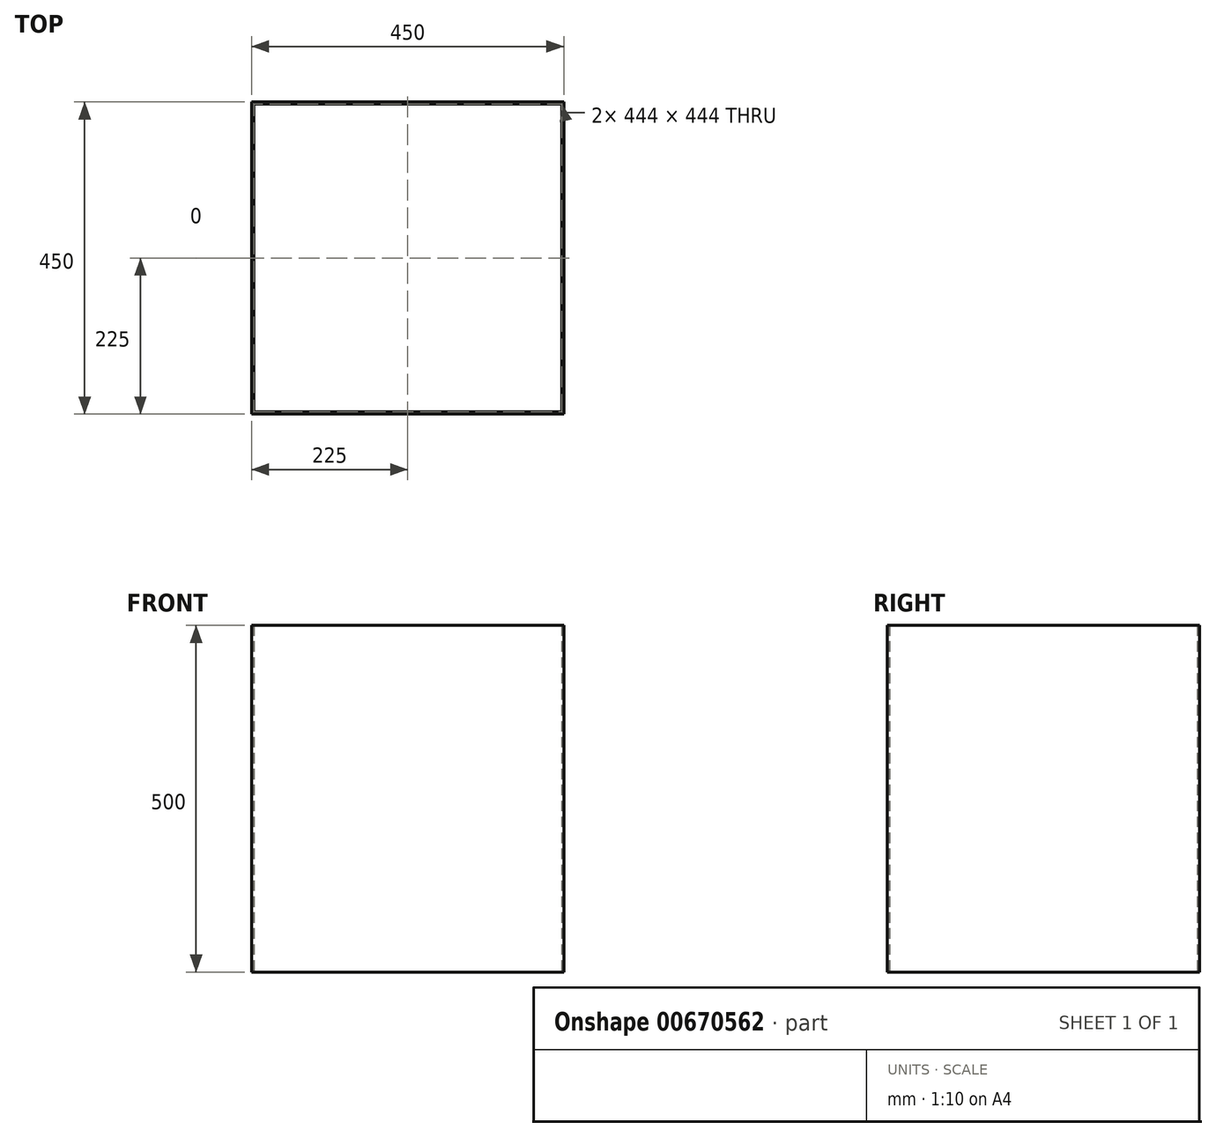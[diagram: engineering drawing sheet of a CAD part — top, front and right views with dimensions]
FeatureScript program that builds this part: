
annotation { "Feature Type Name" : "Feature", "Feature Type Description" : "" }
export const myFeature = defineFeature(function(context is Context, id is Id, definition is map)
    precondition{}
    {
        {
            var Q0;
            Q0=qCreatedBy(makeId("Top.planeOp"),FACE);
            var sketch = newSketch(context, id + "F0", { "sketchPlane" : qUnion([Q0])});
            skLineSegment(sketch, "E0.bottom", {"start": v(225, -225) * mm, "end": v(-225, -225) * mm});
            skLineSegment(sketch, "E0.top", {"start": v(225, 225) * mm, "end": v(-225, 225) * mm});
            skLineSegment(sketch, "E0.left", {"start": v(225, -225) * mm, "end": v(225, 225) * mm});
            skLineSegment(sketch, "E0.right", {"start": v(-225, -225) * mm, "end": v(-225, 225) * mm});
            skPoint(sketch, "E0.middle", {"position": v(0, 0) * mm});
            skLineSegment(sketch, "E1.0", {"start": v(222, 222) * mm, "end": v(-222, 222) * mm});
            skLineSegment(sketch, "E1.1", {"start": v(222, -222) * mm, "end": v(222, 222) * mm});
            skLineSegment(sketch, "E1.2", {"start": v(222, -222) * mm, "end": v(-222, -222) * mm});
            skLineSegment(sketch, "E1.3", {"start": v(-222, -222) * mm, "end": v(-222, 222) * mm});
            skLineSegment(sketch, "E2.0", {"start": v(-230, -230) * mm, "end": v(-230, 225) * mm});
            skLineSegment(sketch, "E2.1", {"start": v(230, -230) * mm, "end": v(-230, -230) * mm});
            skLineSegment(sketch, "E2.2", {"start": v(230, -230) * mm, "end": v(230, 225) * mm});
            skSolve(sketch);
        }
        {
            var Q0;
            Q0=makeQuery(id+"F0.imprint","IMPRINT",FACE,{"disambiguationData":[TD([[makeQuery(id+"F0.imprint","IMPRINT",EDGE,{"derivedFrom":sQuery(id+"F0.wireOp",EDGE,"E0.bottom")}),-1.0]])]});
            extrude(context, id + "F1", {"entities" : qUnion([Q0]), "depth" : 500 * mm, "offsetDistance" : 25 * mm});
        }
    });
